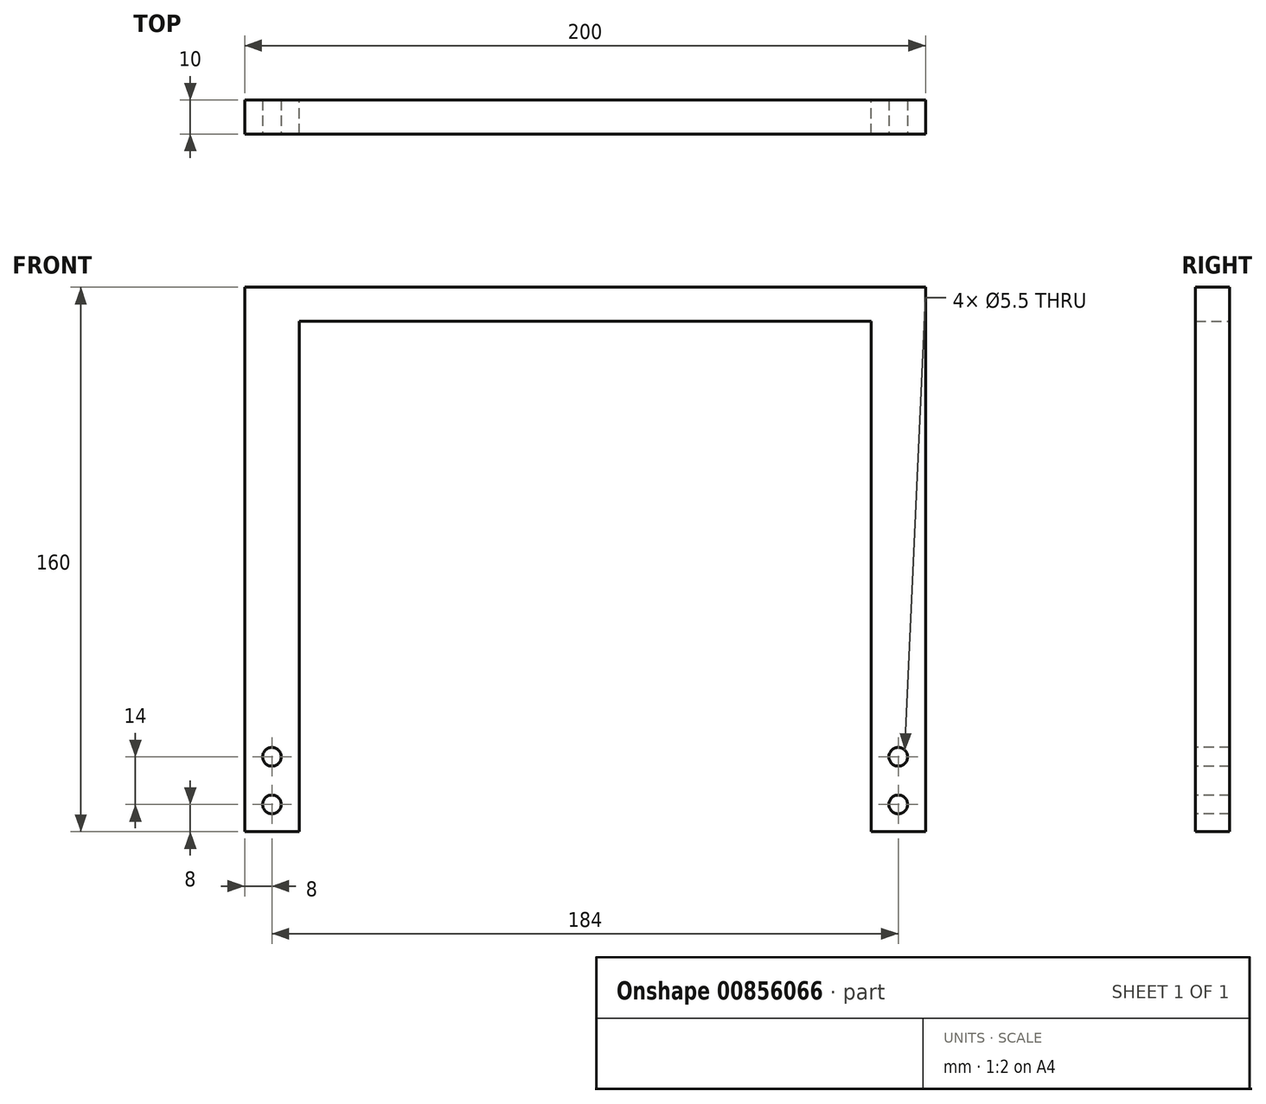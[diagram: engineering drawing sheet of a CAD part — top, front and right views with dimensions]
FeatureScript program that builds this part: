
annotation { "Feature Type Name" : "Feature", "Feature Type Description" : "" }
export const myFeature = defineFeature(function(context is Context, id is Id, definition is map)
    precondition{}
    {
        {
            var Q0;
            Q0=qCreatedBy(makeId("Front.planeOp"),FACE);
            var sketch = newSketch(context, id + "F0", { "sketchPlane" : qUnion([Q0])});
            skLineSegment(sketch, "E0.bottom", {"start": v(100, 5) * mm, "end": v(-100, 5) * mm});
            skLineSegment(sketch, "E0.top", {"start": v(100, -5) * mm, "end": v(-100, -5) * mm});
            skLineSegment(sketch, "E0.left", {"start": v(100, 5) * mm, "end": v(100, -5) * mm});
            skLineSegment(sketch, "E0.right", {"start": v(-100, 5) * mm, "end": v(-100, -5) * mm});
            skPoint(sketch, "E0.middle", {"position": v(0, 0) * mm});
            skLineSegment(sketch, "E1.bottom", {"start": v(-100, -5) * mm, "end": v(-84, -5) * mm});
            skLineSegment(sketch, "E1.top", {"start": v(-100, -155) * mm, "end": v(-84, -155) * mm});
            skLineSegment(sketch, "E1.left", {"start": v(-100, -5) * mm, "end": v(-100, -155) * mm});
            skLineSegment(sketch, "E1.right", {"start": v(-84, -5) * mm, "end": v(-84, -155) * mm});
            skLineSegment(sketch, "E2.bottom", {"start": v(100, -5) * mm, "end": v(84, -5) * mm});
            skLineSegment(sketch, "E2.top", {"start": v(100, -155) * mm, "end": v(84, -155) * mm});
            skLineSegment(sketch, "E2.left", {"start": v(100, -5) * mm, "end": v(100, -155) * mm});
            skLineSegment(sketch, "E2.right", {"start": v(84, -5) * mm, "end": v(84, -155) * mm});
            skSolve(sketch);
        }
        {
            var Q0;
            Q0=makeQuery(id+"F0.imprint","IMPRINT",FACE,{"disambiguationData":[TD([[makeQuery(id+"F0.imprint","IMPRINT",EDGE,{"derivedFrom":sQuery(id+"F0.wireOp",EDGE,"E1.top")}),1.0]])]});
            var Q1;
            Q1=makeQuery(id+"F0.imprint","IMPRINT",FACE,{"disambiguationData":[TD([[makeQuery(id+"F0.imprint","IMPRINT",EDGE,{"derivedFrom":sQuery(id+"F0.wireOp",EDGE,"E2.top")}),-1.0]])]});
            var Q2;
            Q2=makeQuery(id+"F0.imprint","IMPRINT",FACE,{"disambiguationData":[TD([[makeQuery(id+"F0.imprint","IMPRINT",EDGE,{"derivedFrom":sQuery(id+"F0.wireOp",EDGE,"E0.bottom")}),1.0]])]});
            extrude(context, id + "F1", {"entities" : qUnion([Q0, Q1, Q2]), "depth" : 10 * mm, "offsetDistance" : 25 * mm});
        }
        {
            var Q0;
            Q0=makeQuery(id+"F1.opExtrude","CAP_FACE",FACE,{"disambiguationData":[OSD([sQuery(id+"F0.wireOp",EDGE,"E0.bottom"),sQuery(id+"F0.wireOp",EDGE,"E0.top"),sQuery(id+"F0.wireOp",EDGE,"E0.left"),sQuery(id+"F0.wireOp",EDGE,"E0.right"),sQuery(id+"F0.wireOp",EDGE,"E1.top"),sQuery(id+"F0.wireOp",EDGE,"E1.left"),sQuery(id+"F0.wireOp",EDGE,"E1.right"),sQuery(id+"F0.wireOp",EDGE,"E2.top"),sQuery(id+"F0.wireOp",EDGE,"E2.left"),sQuery(id+"F0.wireOp",EDGE,"E2.right")])],"isStart":false});
            var sketch = newSketch(context, id + "F2", { "sketchPlane" : qUnion([Q0])});
            skLineSegment(sketch, "E3", {"start": v(-92, -155) * mm, "end": v(-92, -147) * mm});
            skLineSegment(sketch, "E4", {"start": v(92, -155) * mm, "end": v(92, -147) * mm});
            skLineSegment(sketch, "E5", {"start": v(92, -133) * mm, "end": v(92, -147) * mm});
            skLineSegment(sketch, "E6", {"start": v(-92, -147) * mm, "end": v(-92, -133) * mm});
            skSolve(sketch);
        }
        {
            var Q0;
            Q0=sQuery(id+"F2.wireOp",VERTEX,"E3.end");
            var Q1;
            Q1=sQuery(id+"F2.wireOp",VERTEX,"E6.end");
            var Q2;
            Q2=sQuery(id+"F2.wireOp",VERTEX,"E5.start");
            var Q3;
            Q3=sQuery(id+"F2.wireOp",VERTEX,"E4.end");
            var Q4;
            Q4=makeQuery(id+"F1.opExtrude","SWEPT_BODY",BODY,{"disambiguationData":[OSD([sQuery(id+"F0.wireOp",EDGE,"E0.bottom"),sQuery(id+"F0.wireOp",EDGE,"E0.top"),sQuery(id+"F0.wireOp",EDGE,"E0.left"),sQuery(id+"F0.wireOp",EDGE,"E0.right"),sQuery(id+"F0.wireOp",EDGE,"E1.top"),sQuery(id+"F0.wireOp",EDGE,"E1.left"),sQuery(id+"F0.wireOp",EDGE,"E1.right"),sQuery(id+"F0.wireOp",EDGE,"E2.top"),sQuery(id+"F0.wireOp",EDGE,"E2.left"),sQuery(id+"F0.wireOp",EDGE,"E2.right")])]});
            hole(context, id + "F3", {"style" : HoleStyle.SIMPLE, "endStyle" : HoleEndStyle.THROUGH, "standardTappedOrClearance" : lookupTablePath({ "fit" : "Normal", "standard" : "ISO", "size" : "M5", "type" : "Clearance" }), "standardBlindInLast" : lookupTablePath({ "fit" : "Standard", "standard" : "ISO", "size" : "M5", "type" : "Clearance" }), "holeDiameter" : 5.5 * mm, "majorDiameter" : 5 * mm, "isTappedThrough" : true, "tappedDepth" : 12 * mm, "tapClearance" : 3, "locations" : qUnion([Q0, Q1, Q2, Q3]), "scope" : qUnion([Q4])});
        }
    });
